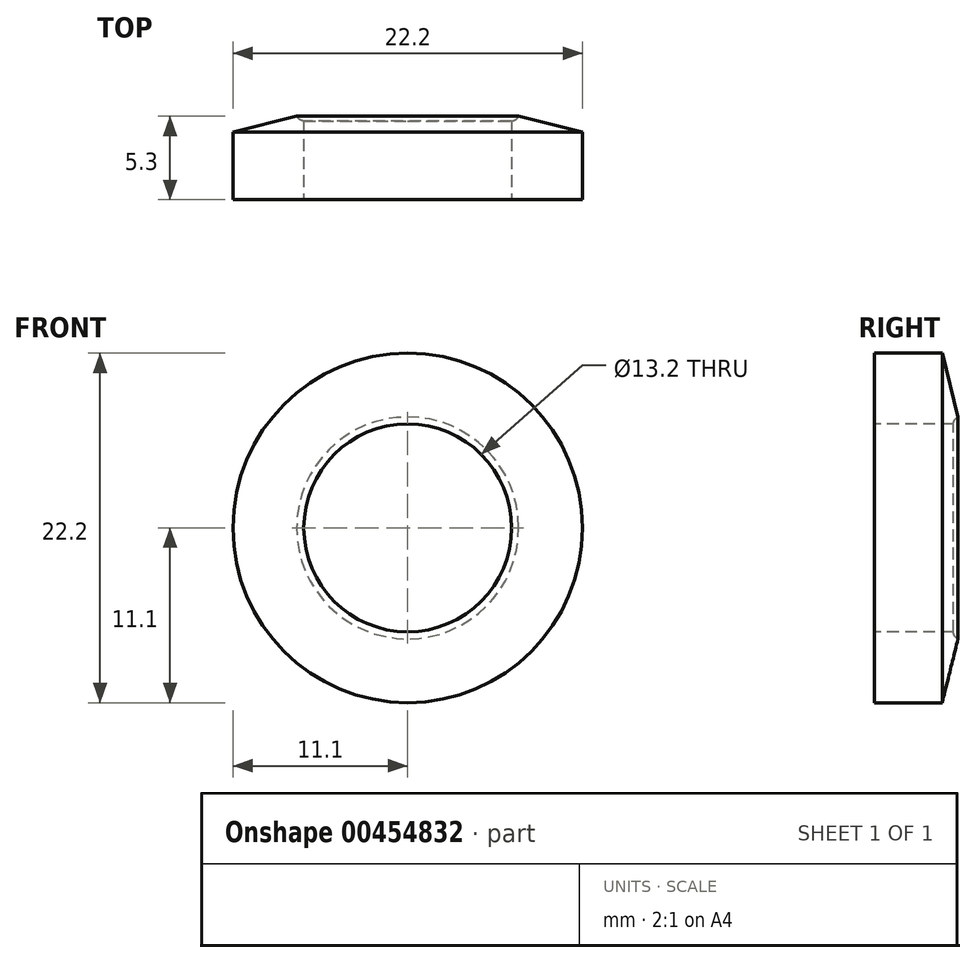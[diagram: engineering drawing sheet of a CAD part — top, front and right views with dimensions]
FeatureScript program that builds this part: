
annotation { "Feature Type Name" : "Feature", "Feature Type Description" : "" }
export const myFeature = defineFeature(function(context is Context, id is Id, definition is map)
    precondition{}
    {
        {
            var Q0;
            Q0=qCreatedBy(makeId("Right.planeOp"),FACE);
            var sketch = newSketch(context, id + "F0", { "sketchPlane" : qUnion([Q0])});
            skLineSegment(sketch, "E0", {"start": v(0, 11.1) * mm, "end": v(0, 6.6) * mm});
            skLineSegment(sketch, "E1", {"start": v(0, 6.6) * mm, "end": v(5, 6.6) * mm});
            skArc(sketch, "E2", {"start": v(5.3, 7.05) * mm, "mid": v(5.1, 6.86) * mm, "end": v(5, 6.6) * mm});
            skLineSegment(sketch, "E3", {"start": v(5.3, 7.05) * mm, "end": v(4.3, 11.1) * mm});
            skLineSegment(sketch, "E4", {"start": v(0, 11.1) * mm, "end": v(4.3, 11.1) * mm});
            skSolve(sketch);
        }
        {
            var Q0;
            Q0=qCreatedBy(makeId("Right.planeOp"),FACE);
            var sketch = newSketch(context, id + "F1", { "sketchPlane" : qUnion([Q0])});
            skLineSegment(sketch, "E5", {"start": v(-36.39, 0) * mm, "end": v(33.4, 0) * mm, "construction": true});
            skSolve(sketch);
        }
        {
            var Q0;
            Q0 = qSketchRegion(id + "F0", true);
            var Q1;
            Q1=sQuery(id+"F1.wireOp",EDGE,"E5");
            revolve(context, id + "F2", {"entities" : qUnion([Q0]), "axis" : qUnion([Q1]), "revolveType" : RevolveType.FULL});
        }
    });
